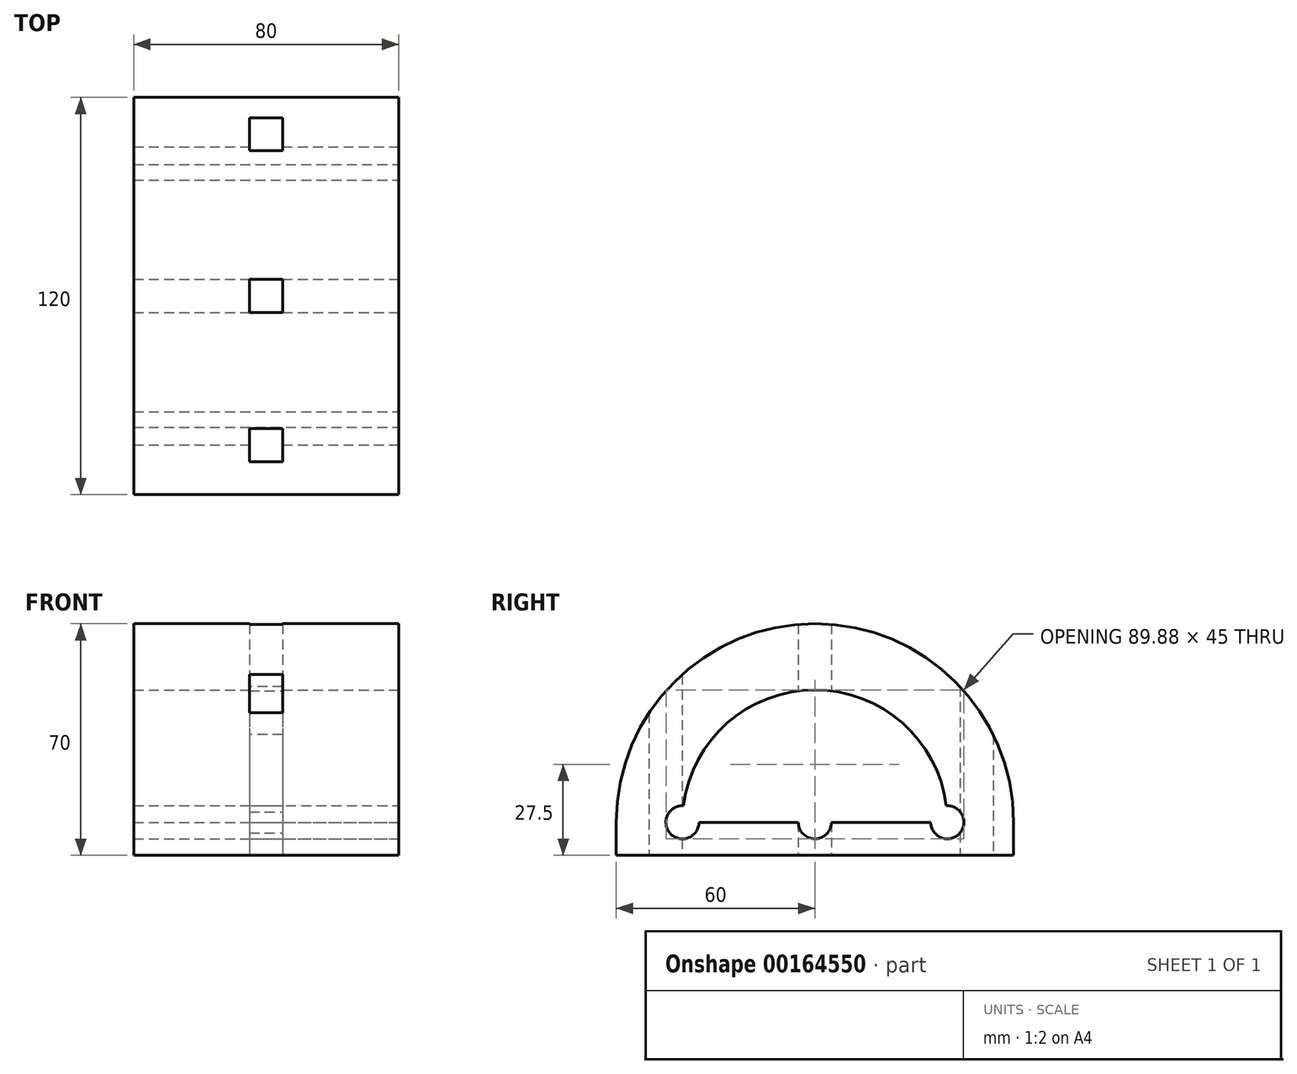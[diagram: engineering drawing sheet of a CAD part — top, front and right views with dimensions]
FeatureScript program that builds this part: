
annotation { "Feature Type Name" : "Feature", "Feature Type Description" : "" }
export const myFeature = defineFeature(function(context is Context, id is Id, definition is map)
    precondition{}
    {
        {
            var Q0;
            Q0=qCreatedBy(makeId("Right.planeOp"),FACE);
            var sketch = newSketch(context, id + "F0", { "sketchPlane" : qUnion([Q0])});
            skLineSegment(sketch, "E0.bottom", {"start": v(-60, -5) * mm, "end": v(60, -5) * mm});
            skLineSegment(sketch, "E0.top", {"start": v(-60, 5) * mm, "end": v(60, 5) * mm});
            skLineSegment(sketch, "E0.left", {"start": v(-60, -5) * mm, "end": v(-60, 5) * mm});
            skLineSegment(sketch, "E0.right", {"start": v(60, -5) * mm, "end": v(60, 5) * mm});
            skPoint(sketch, "E0.middle", {"position": v(0, 0) * mm});
            skArc(sketch, "E1", {"start": v(60, 5) * mm, "mid": v(0, 65) * mm, "end": v(-60, 5) * mm});
            skSolve(sketch);
        }
        {
            var Q0;
            Q0 = qSketchRegion(id + "F0", true);
            extrude(context, id + "F1", {"entities" : qUnion([Q0]), "depth" : 80 * mm});
        }
        {
            var Q0;
            Q0=makeQuery(id+"F1.opExtrude","CAP_FACE",FACE,{"disambiguationData":[OSD([sQuery(id+"F0.wireOp",EDGE,"E0.bottom"),sQuery(id+"F0.wireOp",EDGE,"E0.left"),sQuery(id+"F0.wireOp",EDGE,"E0.right"),sQuery(id+"F0.wireOp",EDGE,"E1")])],"isStart":false});
            var sketch = newSketch(context, id + "F2", { "sketchPlane" : qUnion([Q0])});
            skCircle(sketch, "E2", {"center": v(0, 5) * mm, "radius": 5 * mm});
            skCircle(sketch, "E3", {"center": v(40, 5) * mm, "radius": 5 * mm});
            skCircle(sketch, "E4", {"center": v(-40, 5) * mm, "radius": 5 * mm});
            skArc(sketch, "E5", {"start": v(40, 5) * mm, "mid": v(0, 45) * mm, "end": v(-40, 5) * mm});
            skLineSegment(sketch, "E6", {"start": v(-40, 5) * mm, "end": v(40, 5) * mm});
            skSolve(sketch);
        }
        {
            var Q0;
            Q0 = qSketchRegion(id + "F2", true);
            extrude(context, id + "F3", {"entities" : qUnion([Q0]), "operationType" : NewBodyOperationType.REMOVE, "endBound" : BoundingType.THROUGH_ALL, "oppositeDirection" : true, "depth" : 25 * mm});
        }
        {
            var Q0;
            Q0 = qSketchRegion(id + "F2", true);
            extrude(context, id + "F4", {"entities" : qUnion([Q0]), "operationType" : NewBodyOperationType.REMOVE, "oppositeDirection" : true, "depth" : 25 * mm});
        }
        {
            var Q0;
            Q0=makeQuery(id+"F1.opExtrude","SWEPT_FACE",FACE,{"disambiguationData":[OSD([sQuery(id+"F0.wireOp",EDGE,"E0.bottom")])]});
            var sketch = newSketch(context, id + "F5", { "sketchPlane" : qUnion([Q0])});
            skLineSegment(sketch, "E7.bottom", {"start": v(35, 40.08) * mm, "end": v(45, 40.08) * mm});
            skLineSegment(sketch, "E7.top", {"start": v(35, 50.08) * mm, "end": v(45, 50.08) * mm});
            skLineSegment(sketch, "E7.left", {"start": v(35, 40.08) * mm, "end": v(35, 50.08) * mm});
            skLineSegment(sketch, "E7.right", {"start": v(45, 40.08) * mm, "end": v(45, 50.08) * mm});
            skPoint(sketch, "E7.middle", {"position": v(40, 45.08) * mm});
            skPoint(sketch, "E7.middle.positionSnap0", {"position": v(40, 60) * mm});
            skPoint(sketch, "E7.centerSnap0", {"position": v(40, 60) * mm});
            skLineSegment(sketch, "E8.bottom", {"start": v(35, -5) * mm, "end": v(45, -5) * mm});
            skLineSegment(sketch, "E8.top", {"start": v(35, 5) * mm, "end": v(45, 5) * mm});
            skLineSegment(sketch, "E8.left", {"start": v(35, -5) * mm, "end": v(35, 5) * mm});
            skLineSegment(sketch, "E8.right", {"start": v(45, -5) * mm, "end": v(45, 5) * mm});
            skPoint(sketch, "E8.middle", {"position": v(40, 0) * mm});
            skLineSegment(sketch, "E9.bottom", {"start": v(45, -43.85) * mm, "end": v(35, -43.85) * mm});
            skLineSegment(sketch, "E9.top", {"start": v(45, -53.85) * mm, "end": v(35, -53.85) * mm});
            skLineSegment(sketch, "E9.left", {"start": v(45, -43.85) * mm, "end": v(45, -53.85) * mm});
            skLineSegment(sketch, "E9.right", {"start": v(35, -43.85) * mm, "end": v(35, -53.85) * mm});
            skPoint(sketch, "E9.middle", {"position": v(40, -48.85) * mm});
            skSolve(sketch);
        }
        {
            var Q0;
            Q0 = qSketchRegion(id + "F5", true);
            extrude(context, id + "F6", {"entities" : qUnion([Q0]), "operationType" : NewBodyOperationType.REMOVE, "endBound" : BoundingType.THROUGH_ALL, "oppositeDirection" : true, "depth" : 25 * mm});
        }
    });
